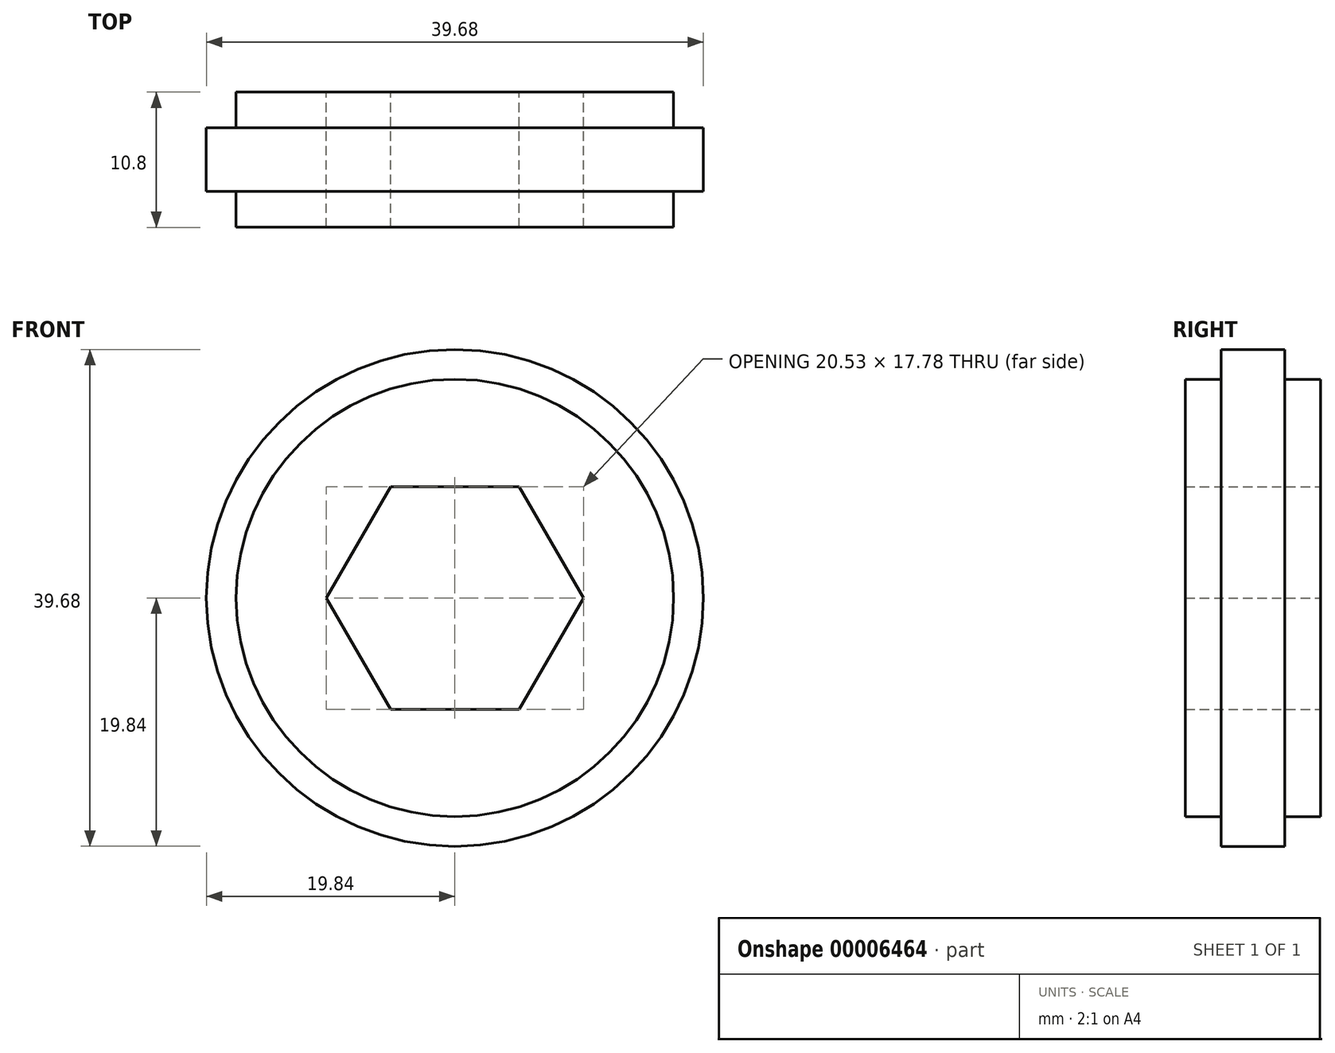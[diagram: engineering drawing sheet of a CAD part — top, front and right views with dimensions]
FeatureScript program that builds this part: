
annotation { "Feature Type Name" : "Feature", "Feature Type Description" : "" }
export const myFeature = defineFeature(function(context is Context, id is Id, definition is map)
    precondition{}
    {
        {
            var Q0;
            Q0=qCreatedBy(makeId("Front.planeOp"),FACE);
            var sketch = newSketch(context, id + "F0", { "sketchPlane" : qUnion([Q0])});
            skCircle(sketch, "E0.cCircle", {"center": v(0, 0) * mm, "radius": 8.9 * mm, "construction": true});
            skLineSegment(sketch, "E0.0", {"start": v(5.13, 8.9) * mm, "end": v(10.27, 0) * mm});
            skLineSegment(sketch, "E0.1", {"start": v(10.27, 0) * mm, "end": v(5.13, -8.89) * mm});
            skLineSegment(sketch, "E0.2", {"start": v(5.13, -8.89) * mm, "end": v(-5.13, -8.89) * mm});
            skLineSegment(sketch, "E0.3", {"start": v(-5.13, -8.9) * mm, "end": v(-10.27, 0) * mm});
            skLineSegment(sketch, "E0.4", {"start": v(-10.27, 0) * mm, "end": v(-5.13, 8.9) * mm});
            skLineSegment(sketch, "E0.5", {"start": v(-5.13, 8.9) * mm, "end": v(5.13, 8.9) * mm});
            skPoint(sketch, "E0.0.midPoint", {"position": v(7.7, 4.45) * mm});
            skCircle(sketch, "E1", {"center": v(0, 0) * mm, "radius": 17.46 * mm});
            skSolve(sketch);
        }
        {
            var Q0;
            Q0 = qSketchRegion(id + "F0", true);
            extrude(context, id + "F1", {"entities" : qUnion([Q0]), "depth" : 10.8 * mm});
        }
        {
            var Q0;
            Q0=qCreatedBy(makeId("Right.planeOp"),FACE);
            var sketch = newSketch(context, id + "F2", { "sketchPlane" : qUnion([Q0])});
            skLineSegment(sketch, "E2.bottom", {"start": v(-7.94, 17.46) * mm, "end": v(-2.86, 17.46) * mm});
            skLineSegment(sketch, "E2.top", {"start": v(-7.94, 19.84) * mm, "end": v(-2.86, 19.84) * mm});
            skLineSegment(sketch, "E2.left", {"start": v(-7.94, 17.46) * mm, "end": v(-7.94, 19.84) * mm});
            skLineSegment(sketch, "E2.right", {"start": v(-2.86, 17.46) * mm, "end": v(-2.86, 19.84) * mm});
            skLineSegment(sketch, "E3", {"start": v(0, 0) * mm, "end": v(-17.08, 0) * mm, "construction": true});
            skSolve(sketch);
        }
        {
            var Q0;
            Q0 = qSketchRegion(id + "F2", true);
            var Q1;
            Q1=sQuery(id+"F2.wireOp",EDGE,"E3");
            revolve(context, id + "F3", {"operationType" : NewBodyOperationType.ADD, "entities" : qUnion([Q0]), "axis" : qUnion([Q1]), "revolveType" : RevolveType.FULL});
        }
    });
